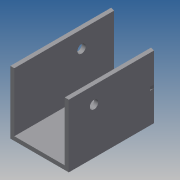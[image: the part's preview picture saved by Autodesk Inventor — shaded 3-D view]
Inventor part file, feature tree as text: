
AUTODESK INVENTOR PART (.ipt)
format: ipt  version: 2014 SP1 (Build 180222100, 222)  size: 109,568 bytes
history: native  units: in
note: dims shown in document units (in); Inventor stores cm internally (conversion verified against a paired STEP export)
features: sketch x5, extrude x3, hole x2, plane x1
ambient origin geometry x8: Origin, YZ Plane, XZ Plane, XY Plane, X Axis, Y Axis, Z Axis, Center Point
bodies: Solid1 (feature_tree)
feature tree (11):
  extrude  "channel"  Depth=1.75in
  extrude  "angleCut"  Depth=0.12in
  hole  "Hole1"  [1 undecoded]
  hole  "Hole2"  [1 undecoded]
  plane  "Work Plane1"
  extrude  "indentMark"  Depth=0.1in
  sketch  "Sketch1"  dims[d0=1.5in d1=1.75in]
  sketch  "Sketch2"  dims[d2=1.75in d3=0.12in]
  sketch  "Sketch3"  dims[d4=3.0in d5=0.0in d6=2.0in]
  sketch  "Sketch5"  dims[d7=15.0deg d8=4.0in d9=0.0in]
  sketch  "Sketch6"  dims[d10=0.75in d11=0.5in d12=0.25in d13=0.75in d14=0.375in d15=0.25in d16=0.5635in d17=1.0in d18=0.8108in d19=2.0in d20=0.5in d21=0.25in d22=0.75in d23=0.375in d24=0.25in d25=0.5635in d26=1.0in d27=0.8108in d28=90.0deg d29=0.1in d30=0.1in d31=4.0in d32=0.0in]
note: 2 required parameter values undecoded (feature->parameter linkage not recoverable at this tier; creation-order binding heuristic only, values carry confidence <= 0.55)
